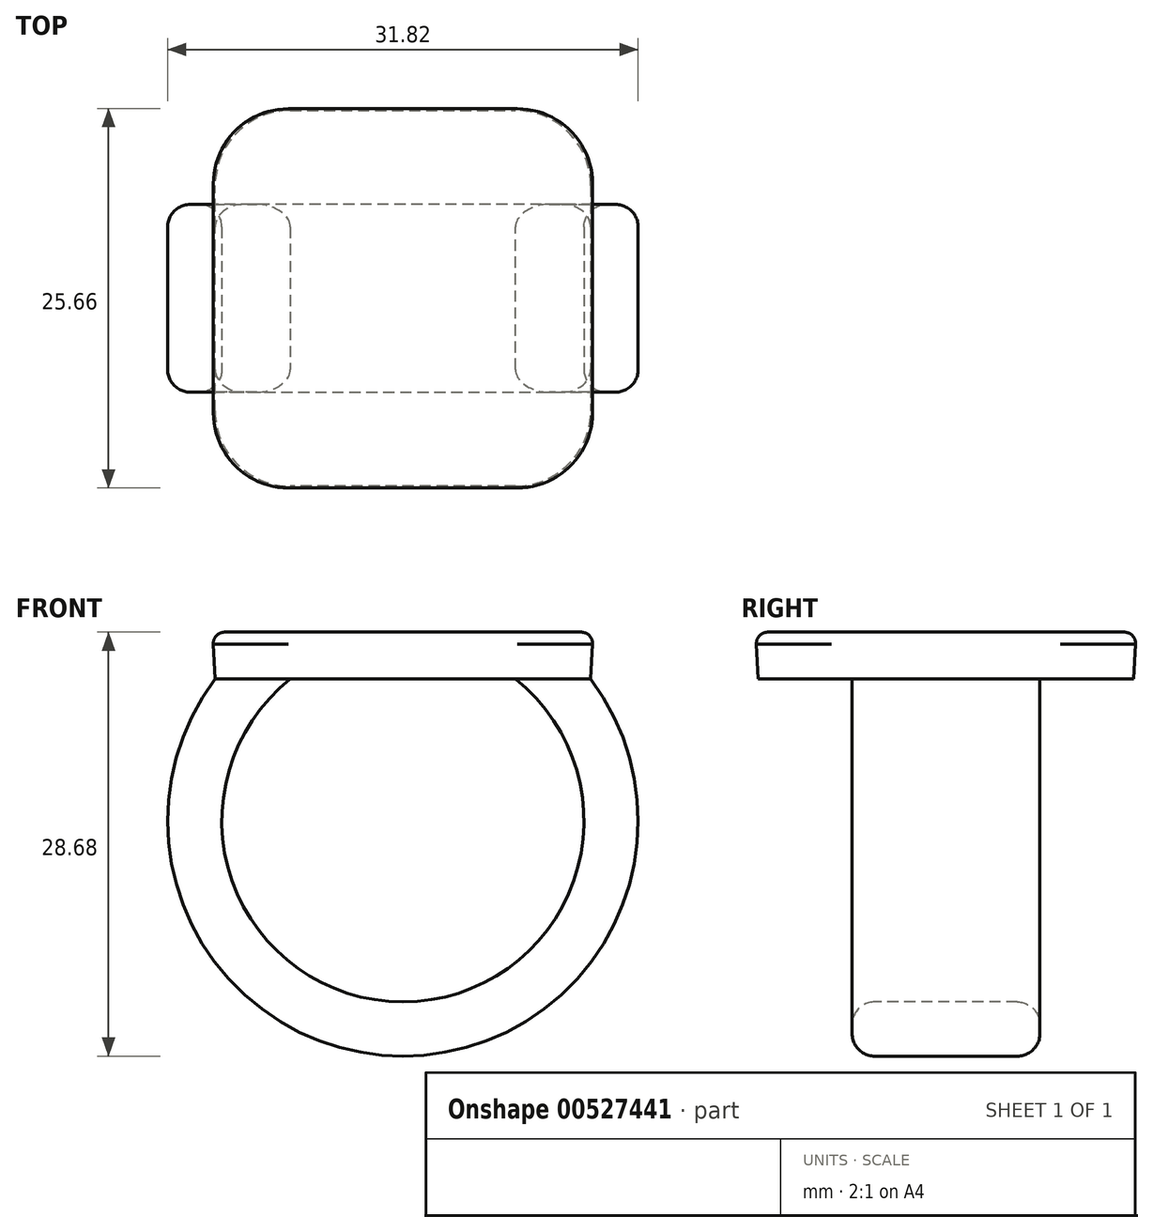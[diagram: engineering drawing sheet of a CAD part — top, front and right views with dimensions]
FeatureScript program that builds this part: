
annotation { "Feature Type Name" : "Feature", "Feature Type Description" : "" }
export const myFeature = defineFeature(function(context is Context, id is Id, definition is map)
    precondition{}
    {
        {
            var Q0;
            Q0=qCreatedBy(makeId("Top.planeOp"),FACE);
            var sketch = newSketch(context, id + "F0", { "sketchPlane" : qUnion([Q0])});
            skLineSegment(sketch, "E0.bottom", {"start": v(12.7, -12.7) * mm, "end": v(-12.7, -12.7) * mm});
            skLineSegment(sketch, "E0.top", {"start": v(12.7, 12.7) * mm, "end": v(-12.7, 12.7) * mm});
            skLineSegment(sketch, "E0.left", {"start": v(12.7, -12.7) * mm, "end": v(12.7, 12.7) * mm});
            skLineSegment(sketch, "E0.right", {"start": v(-12.7, -12.7) * mm, "end": v(-12.7, 12.7) * mm});
            skPoint(sketch, "E0.middle", {"position": v(0, 0) * mm});
            skSolve(sketch);
        }
        {
            var Q0;
            Q0 = qSketchRegion(id + "F0", true);
            extrude(context, id + "F1", {"entities" : qUnion([Q0]), "depth" : 3.17 * mm, "offsetDistance" : 25.4 * mm, "hasDraft" : true, "draftAngle" : 3 * degree});
        }
        {
            var Q0;
            Q0=qCreatedBy(makeId("Front.planeOp"),FACE);
            var sketch = newSketch(context, id + "F2", { "sketchPlane" : qUnion([Q0])});
            skArc(sketch, "E1", {"start": v(-10.16, 0) * mm, "mid": v(0, -23.56) * mm, "end": v(10.16, 0) * mm});
            skSolve(sketch);
        }
        {
            var Q0;
            Q0=makeQuery(id+"F1.opExtrude","CAP_FACE",FACE,{"disambiguationData":[OSD([sQuery(id+"F0.wireOp",EDGE,"E0.bottom"),sQuery(id+"F0.wireOp",EDGE,"E0.top"),sQuery(id+"F0.wireOp",EDGE,"E0.left"),sQuery(id+"F0.wireOp",EDGE,"E0.right")])],"isStart":true});
            var sketch = newSketch(context, id + "F3", { "sketchPlane" : qUnion([Q0])});
            skLineSegment(sketch, "E2.bottom", {"start": v(-7.62, -6.35) * mm, "end": v(-12.7, -6.35) * mm});
            skLineSegment(sketch, "E2.top", {"start": v(-7.62, 6.35) * mm, "end": v(-12.7, 6.35) * mm});
            skLineSegment(sketch, "E2.left", {"start": v(-7.62, -6.35) * mm, "end": v(-7.62, 6.35) * mm});
            skLineSegment(sketch, "E2.right", {"start": v(-12.7, -6.35) * mm, "end": v(-12.7, 6.35) * mm});
            skPoint(sketch, "E2.middle", {"position": v(-10.16, 0) * mm});
            skSolve(sketch);
        }
        {
            var Q0;
            Q0 = qSketchRegion(id + "F3", true);
            var Q1;
            Q1 = qConstructionFilter(qBodyType(qCreatedBy(id + "F2" ,EDGE), BodyType.WIRE), ConstructionObject.NO);
            sweep(context, id + "F4", {"operationType" : NewBodyOperationType.ADD, "profiles" : qUnion([Q0]), "path" : qUnion([Q1])});
        }
        {
            var Q0;
            Q0=qCreatedBy(makeId("Front.planeOp"),FACE);
            var sketch = newSketch(context, id + "F5", { "sketchPlane" : qUnion([Q0])});
            skLineSegment(sketch, "E3.0", {"start": v(10.16, 0) * mm, "end": v(7.62, 0) * mm});
            skLineSegment(sketch, "E3.1", {"start": v(10.01, -2.54) * mm, "end": v(10.16, 0) * mm});
            skArc(sketch, "E3.2", {"start": v(10.01, -2.54) * mm, "mid": v(8.9, -1.18) * mm, "end": v(7.62, 0) * mm});
            skPoint(sketch, "E4.orphan", {"position": v(-7.62, 0) * mm});
            skPoint(sketch, "E5.orphan", {"position": v(-12.7, 0) * mm});
            skPoint(sketch, "E6.orphan", {"position": v(12.7, 0) * mm});
            skSolve(sketch);
        }
        {
            var Q0;
            Q0 = qSketchRegion(id + "F5", true);
            var Q1;
            Q1=makeQuery(id+"F4.opSweep","SWEPT_FACE",FACE,{"disambiguationData":[OSD([sQuery(id+"F2.wireOp",EDGE,"E1"),sQuery(id+"F3.wireOp",EDGE,"E2.top")])]});
            var Q2;
            Q2=makeQuery(id+"F4.opSweep","SWEPT_FACE",FACE,{"disambiguationData":[OSD([sQuery(id+"F2.wireOp",EDGE,"E1"),sQuery(id+"F3.wireOp",EDGE,"E2.bottom")])]});
            extrude(context, id + "F6", {"entities" : qUnion([Q0]), "operationType" : NewBodyOperationType.ADD, "endBound" : BoundingType.UP_TO_SURFACE, "depth" : 25.4 * mm, "endBoundEntityFace" : qUnion([Q1]), "offsetDistance" : 25.4 * mm, "hasSecondDirection" : true, "secondDirectionBound" : SecondDirectionBoundingType.UP_TO_SURFACE, "secondDirectionOppositeDirection" : true, "secondDirectionDepth" : 25.4 * mm, "secondDirectionBoundEntityFace" : qUnion([Q2])});
        }
        {
            var Q0;
            Q0=makeQuery(id+"F1.opExtrude","SWEPT_EDGE",EDGE,{"disambiguationData":[OSD([sQuery(id+"F0.wireOp",EDGE,"E0.bottom"),sQuery(id+"F0.wireOp",EDGE,"E0.left")])]});
            var Q1;
            Q1=makeQuery(id+"F1.opExtrude","SWEPT_EDGE",EDGE,{"disambiguationData":[OSD([sQuery(id+"F0.wireOp",EDGE,"E0.top"),sQuery(id+"F0.wireOp",EDGE,"E0.left")])]});
            var Q2;
            Q2=makeQuery(id+"F1.opExtrude","SWEPT_EDGE",EDGE,{"disambiguationData":[OSD([sQuery(id+"F0.wireOp",EDGE,"E0.top"),sQuery(id+"F0.wireOp",EDGE,"E0.right")])]});
            var Q3;
            Q3=makeQuery(id+"F1.opExtrude","SWEPT_EDGE",EDGE,{"disambiguationData":[OSD([sQuery(id+"F0.wireOp",EDGE,"E0.bottom"),sQuery(id+"F0.wireOp",EDGE,"E0.right")])]});
            fillet(context, id + "F7", {"entities" : qUnion([Q0, Q1, Q2, Q3]), "radius" : 5.08 * mm, "tangentPropagation" : true, "allowEdgeOverflow" : false});
        }
        {
            var Q0;
            {var subQ0=sQuery(id+"F3.wireOp",EDGE,"E2.bottom");var subQ1=sQuery(id+"F2.wireOp",EDGE,"E1");Q0=makeQuery(id+"F6.boolean.opBoolean","MERGE",EDGE,{"derivedFrom":[makeQuery(id+"F4.opSweep","SWEPT_EDGE",EDGE,{"disambiguationData":[OSD([subQ1,subQ0,sQuery(id+"F3.wireOp",EDGE,"E2.left")])]}),makeQuery(id+"F6.opExtrude","TWEAK_EDGE",EDGE,{"derivedFrom":[makeQuery(id+"F4.opSweep","SWEPT_FACE",FACE,{"disambiguationData":[OSD([subQ1,subQ0])]}),makeQuery(id+"F5.imprint","IMPRINT",EDGE,{"derivedFrom":sQuery(id+"F5.wireOp",EDGE,"E3.2")})]})]});}
            var Q1;
            Q1=makeQuery(id+"F4.opSweep","SWEPT_EDGE",EDGE,{"disambiguationData":[OSD([sQuery(id+"F0.wireOp",EDGE,"E0.right"),sQuery(id+"F2.wireOp",EDGE,"E1"),sQuery(id+"F3.wireOp",EDGE,"E2.bottom"),sQuery(id+"F3.wireOp",EDGE,"E2.right")])]});
            var Q2;
            Q2=makeQuery(id+"F4.opSweep","SWEPT_EDGE",EDGE,{"disambiguationData":[OSD([sQuery(id+"F0.wireOp",EDGE,"E0.right"),sQuery(id+"F2.wireOp",EDGE,"E1"),sQuery(id+"F3.wireOp",EDGE,"E2.top"),sQuery(id+"F3.wireOp",EDGE,"E2.right")])]});
            var Q3;
            {var subQ0=sQuery(id+"F3.wireOp",EDGE,"E2.top");var subQ1=sQuery(id+"F2.wireOp",EDGE,"E1");Q3=makeQuery(id+"F6.boolean.opBoolean","MERGE",EDGE,{"derivedFrom":[makeQuery(id+"F4.opSweep","SWEPT_EDGE",EDGE,{"disambiguationData":[OSD([subQ1,subQ0,sQuery(id+"F3.wireOp",EDGE,"E2.left")])]}),makeQuery(id+"F6.opExtrude","TWEAK_EDGE",EDGE,{"derivedFrom":[makeQuery(id+"F4.opSweep","SWEPT_FACE",FACE,{"disambiguationData":[OSD([subQ1,subQ0])]}),makeQuery(id+"F5.imprint","IMPRINT",EDGE,{"derivedFrom":sQuery(id+"F5.wireOp",EDGE,"E3.2")})]})]});}
            fillet(context, id + "F8", {"entities" : qUnion([Q0, Q1, Q2, Q3]), "radius" : 1.52 * mm, "tangentPropagation" : true, "allowEdgeOverflow" : false});
        }
        {
            var Q0;
            Q0=makeQuery(id+"F1.opExtrude","CAP_FACE",FACE,{"disambiguationData":[OSD([sQuery(id+"F0.wireOp",EDGE,"E0.bottom"),sQuery(id+"F0.wireOp",EDGE,"E0.top"),sQuery(id+"F0.wireOp",EDGE,"E0.left"),sQuery(id+"F0.wireOp",EDGE,"E0.right")])],"isStart":false});
            fillet(context, id + "F9", {"entities" : qUnion([Q0]), "radius" : 0.76 * mm, "tangentPropagation" : true, "allowEdgeOverflow" : false});
        }
    });
